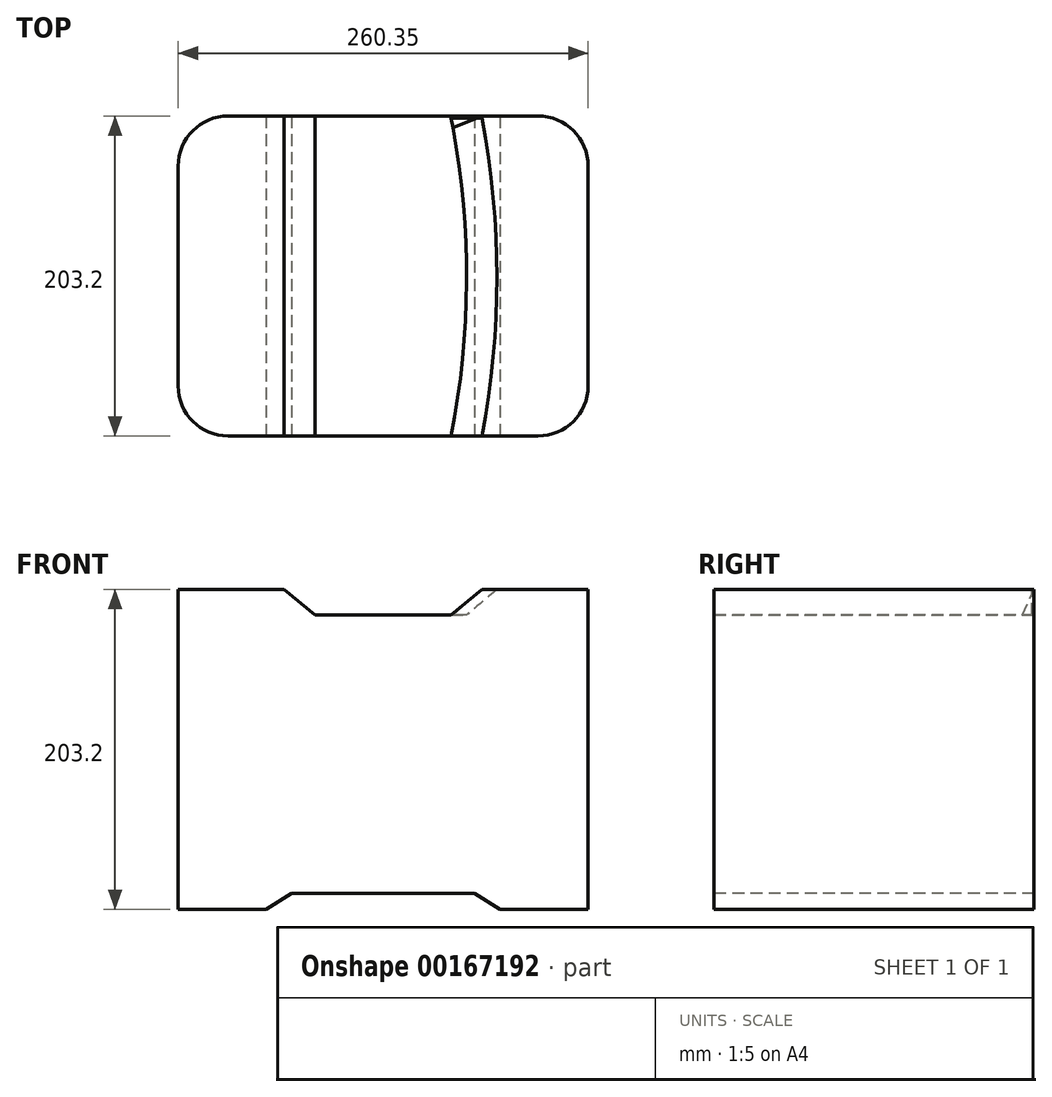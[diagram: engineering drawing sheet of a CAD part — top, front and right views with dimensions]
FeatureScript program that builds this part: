
annotation { "Feature Type Name" : "Feature", "Feature Type Description" : "" }
export const myFeature = defineFeature(function(context is Context, id is Id, definition is map)
    precondition{}
    {
        {
            var Q0;
            Q0=qCreatedBy(makeId("Top.planeOp"),FACE);
            var sketch = newSketch(context, id + "F0", { "sketchPlane" : qUnion([Q0])});
            skLineSegment(sketch, "E0.bottom", {"start": v(-173.4, 109.22) * mm, "end": v(86.96, 109.22) * mm});
            skLineSegment(sketch, "E0.top", {"start": v(-173.4, -93.98) * mm, "end": v(86.96, -93.98) * mm});
            skLineSegment(sketch, "E0.left", {"start": v(-173.4, 109.22) * mm, "end": v(-173.4, -93.98) * mm});
            skLineSegment(sketch, "E0.right", {"start": v(86.96, 109.22) * mm, "end": v(86.96, -93.98) * mm});
            skSolve(sketch);
        }
        {
            var Q0;
            Q0=makeQuery(id+"F0.imprint","IMPRINT",FACE,{"disambiguationData":[TD([[makeQuery(id+"F0.imprint","IMPRINT",EDGE,{"derivedFrom":sQuery(id+"F0.wireOp",EDGE,"E0.bottom")}),-1.0]])]});
            extrude(context, id + "F1", {"entities" : qUnion([Q0]), "depth" : 203.2 * mm});
        }
        {
            var Q0;
            Q0=makeQuery(id+"F1.opExtrude","SWEPT_EDGE",EDGE,{"disambiguationData":[OSD([sQuery(id+"F0.wireOp",EDGE,"E0.bottom"),sQuery(id+"F0.wireOp",EDGE,"E0.left")])]});
            var Q1;
            Q1=makeQuery(id+"F1.opExtrude","SWEPT_EDGE",EDGE,{"disambiguationData":[OSD([sQuery(id+"F0.wireOp",EDGE,"E0.top"),sQuery(id+"F0.wireOp",EDGE,"E0.left")])]});
            var Q2;
            Q2=makeQuery(id+"F1.opExtrude","SWEPT_EDGE",EDGE,{"disambiguationData":[OSD([sQuery(id+"F0.wireOp",EDGE,"E0.bottom"),sQuery(id+"F0.wireOp",EDGE,"E0.right")])]});
            var Q3;
            Q3=makeQuery(id+"F1.opExtrude","SWEPT_EDGE",EDGE,{"disambiguationData":[OSD([sQuery(id+"F0.wireOp",EDGE,"E0.top"),sQuery(id+"F0.wireOp",EDGE,"E0.right")])]});
            fillet(context, id + "F2", {"entities" : qUnion([Q0, Q1, Q2, Q3]), "radius" : 31.75 * mm, "tangentPropagation" : true, "allowEdgeOverflow" : false});
        }
        {
            var Q0;
            Q0=makeQuery(id+"F1.opExtrude","SWEPT_FACE",FACE,{"disambiguationData":[OSD([sQuery(id+"F0.wireOp",EDGE,"E0.top")])]});
            var sketch = newSketch(context, id + "F3", { "sketchPlane" : qUnion([Q0])});
            skLineSegment(sketch, "E1", {"start": v(-106.08, 203.2) * mm, "end": v(-86.43, 187.1) * mm});
            skLineSegment(sketch, "E2", {"start": v(-86.43, 187.1) * mm, "end": v(0, 187.1) * mm});
            skLineSegment(sketch, "E3", {"start": v(0, 187.1) * mm, "end": v(19.65, 203.2) * mm});
            skLineSegment(sketch, "E4", {"start": v(-117.51, 0) * mm, "end": v(-101.36, 10.1) * mm});
            skLineSegment(sketch, "E5", {"start": v(-101.36, 10.1) * mm, "end": v(14.95, 10.1) * mm});
            skLineSegment(sketch, "E6", {"start": v(14.95, 10.1) * mm, "end": v(31.1, 0) * mm});
            skLineSegment(sketch, "E7", {"start": v(-117.51, 0) * mm, "end": v(31.1, 0) * mm});
            skSolve(sketch);
        }
        {
            var Q0;
            {var subQ0=sQuery(id+"F3.wireOp",EDGE,"E1");Q0=makeQuery(id+"F3.imprint","IMPRINT",FACE,{"disambiguationData":[TD([[makeQuery(id+"F3.imprint","IMPRINT",EDGE,{"derivedFrom":subQ0}),1.0]])]});}
            var Q1;
            Q1=makeQuery(id+"F3.imprint","IMPRINT",FACE,{"disambiguationData":[TD([[makeQuery(id+"F3.imprint","IMPRINT",EDGE,{"derivedFrom":sQuery(id+"F3.wireOp",EDGE,"E4")}),-1.0]])]});
            extrude(context, id + "F4", {"entities" : qUnion([Q0, Q1]), "operationType" : NewBodyOperationType.REMOVE, "endBound" : BoundingType.THROUGH_ALL, "oppositeDirection" : true, "depth" : 241.3 * mm});
        }
        {
            var Q0;
            {var subQ0=sQuery(id+"F0.wireOp",EDGE,"E0.left");var subQ1=sQuery(id+"F0.wireOp",EDGE,"E0.bottom");var subQ2=sQuery(id+"F0.wireOp",EDGE,"E0.top");Q0=makeQuery(id+"F4.boolean.opBoolean","SPLIT",FACE,{"disambiguationData":[TD([makeQuery(id+"F1.opExtrude","SWEPT_FACE",FACE,{"disambiguationData":[OSD([subQ0])]})])],"derivedFrom":makeQuery(id+"F1.opExtrude","CAP_FACE",FACE,{"disambiguationData":[OSD([subQ1,subQ2,subQ0,sQuery(id+"F0.wireOp",EDGE,"E0.right")])],"isStart":false})});}
            var sketch = newSketch(context, id + "F5", { "sketchPlane" : qUnion([Q0])});
            skArc(sketch, "E8", {"start": v(-106.08, 109.22) * mm, "mid": v(-116.07, 7.62) * mm, "end": v(-106.08, -93.98) * mm});
            skArc(sketch, "E9", {"start": v(20.04, -93.98) * mm, "mid": v(29.43, 7.63) * mm, "end": v(19.78, 109.22) * mm});
            skLineSegment(sketch, "E10", {"start": v(-106.08, -93.98) * mm, "end": v(-105.42, -97.3) * mm});
            skLineSegment(sketch, "E11", {"start": v(-106.08, 109.22) * mm, "end": v(-100.9, 135.33) * mm});
            skLineSegment(sketch, "E12", {"start": v(19.78, 109.22) * mm, "end": v(14.25, 138.24) * mm});
            skSolve(sketch);
        }
        {
            var Q0;
            Q0=makeQuery(id+"F1.opExtrude","SWEPT_FACE",FACE,{"disambiguationData":[OSD([sQuery(id+"F0.wireOp",EDGE,"E0.top")])]});
            var sketch = newSketch(context, id + "F6", { "sketchPlane" : qUnion([Q0])});
            skLineSegment(sketch, "E13", {"start": v(19.65, 203.2) * mm, "end": v(0, 203.2) * mm});
            skLineSegment(sketch, "E14", {"start": v(0, 187.1) * mm, "end": v(19.65, 203.2) * mm});
            skLineSegment(sketch, "E15", {"start": v(0, 187.1) * mm, "end": v(-25.1, 187.1) * mm});
            skLineSegment(sketch, "E16", {"start": v(-25.1, 187.1) * mm, "end": v(-25.1, 203.33) * mm});
            skLineSegment(sketch, "E17", {"start": v(-25.1, 203.33) * mm, "end": v(0, 203.2) * mm});
            skSolve(sketch);
        }
        {
            var Q0;
            Q0=makeQuery(id+"F6.imprint","IMPRINT",FACE,{"disambiguationData":[TD([[makeQuery(id+"F6.imprint","IMPRINT",EDGE,{"derivedFrom":sQuery(id+"F6.wireOp",EDGE,"E13")}),1.0]])]});
            var Q1;
            Q1=sQuery(id+"F5.wireOp",EDGE,"E9");
            var Q2;
            Q2=sQuery(id+"F5.wireOp",EDGE,"E12");
            sweep(context, id + "F7", {"operationType" : NewBodyOperationType.REMOVE, "profiles" : qUnion([Q0]), "path" : qUnion([Q1, Q2])});
        }
    });
